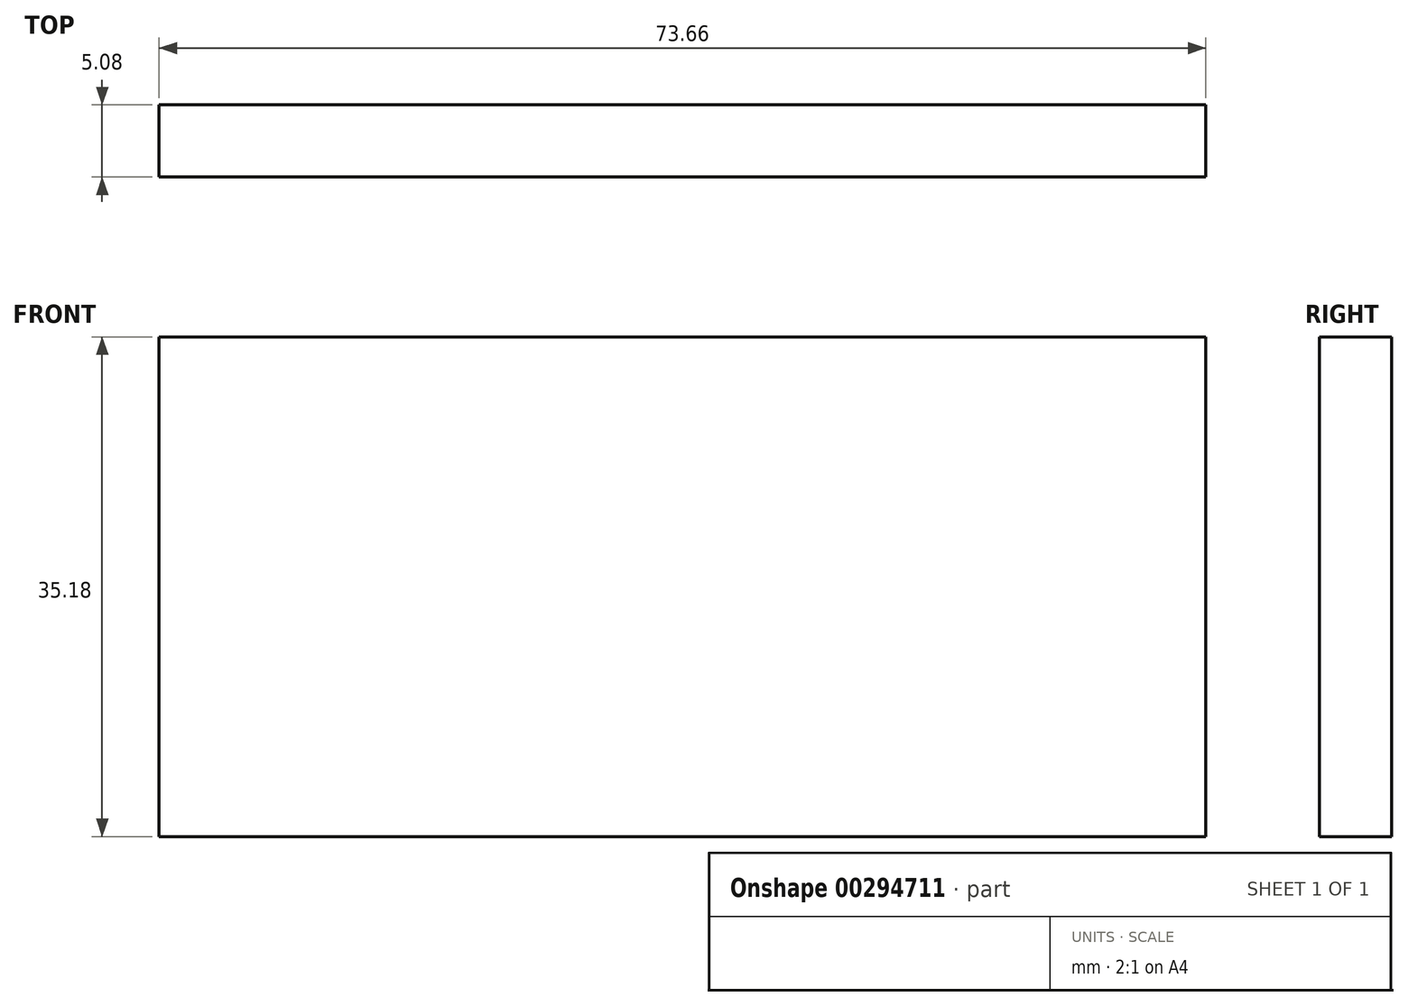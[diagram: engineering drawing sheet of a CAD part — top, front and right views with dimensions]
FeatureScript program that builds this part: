
annotation { "Feature Type Name" : "Feature", "Feature Type Description" : "" }
export const myFeature = defineFeature(function(context is Context, id is Id, definition is map)
    precondition{}
    {
        {
            var Q0;
            Q0=qCreatedBy(makeId("Front.planeOp"),FACE);
            var sketch = newSketch(context, id + "F0", { "sketchPlane" : qUnion([Q0])});
            skLineSegment(sketch, "E0.bottom", {"start": v(0, 0) * mm, "end": v(73.66, 0) * mm});
            skLineSegment(sketch, "E0.top", {"start": v(0, 35.18) * mm, "end": v(73.66, 35.18) * mm});
            skLineSegment(sketch, "E0.left", {"start": v(0, 0) * mm, "end": v(0, 35.18) * mm});
            skLineSegment(sketch, "E0.right", {"start": v(73.66, 0) * mm, "end": v(73.66, 35.18) * mm});
            skSolve(sketch);
        }
        {
            var Q0;
            Q0 = qSketchRegion(id + "F0", true);
            extrude(context, id + "F1", {"entities" : qUnion([Q0]), "depth" : 5.08 * mm});
        }
    });
